# Revit family: FP_Revit_18_VB30SPEX1_Vacuum_Drawer_9000xxxxA
name_source: partatom
category: Specialty Equipment
revit_build: Autodesk Revit 2018 (Build: 20170223_1515(x64)
units: mm (PartAtom-declared; Revit-internal decimal feet)

## family parameters
Always vertical = Yes
Cut with Voids When Loaded = Yes
OmniClass Number = 23.40.40.14.17.31
OmniClass Title = Small Specialized Cooking Equipment
Part Type = Normal
Room Calculation Point = No
Round Connector Dimension = Use Diameter
Shared = No
Work Plane-Based = No

## types (1)
- VB30SPEX1
    Cavity - Depth = 560 mm  [stored 1.83727 ft]
    Cavity - Height = 273 mm  [stored 0.895669 ft]
    Cavity - Width = 724 mm  [stored 2.37533 ft]
    Chassis - Depth = 551 mm  [stored 1.80774 ft]
    Chassis - Height = 271 mm  [stored 0.889108 ft]
    Chassis - Width = 720 mm  [stored 2.3622 ft]
    Connector Description - Electrical = 110 V, 60Hz, 10 A
    Description = 30" Vacuum Drawer
    Manufacturer = Fisher & Paykel Appliances
    Material - Body = Fisher & Paykel - Grey
    Material - Front = Fisher & Paykel - Stainless Steel
    Material - Handle = Fisher & Paykel - Stainless Steel
    Material - Structure = Fisher & Paykel - Black
    Material - Trim = Fisher & Paykel - Black
    Model = VB30SPEX1
    Product - Depth = 630 mm  [stored 2.06693 ft]
    Product - Height = 271 mm  [stored 0.889108 ft]
    Product - Width = 761 mm  [stored 2.49672 ft]
    URL = www.fisherpaykel.com
    Visibility - Clearance Required = Yes

note: [stored X ft] marks values corroborated as IEEE doubles in the binary element streams (Revit-internal decimal feet)

## geometry (parser evidence)
native form markers: Sweep x5
no freeform markers — native parametric forms only
